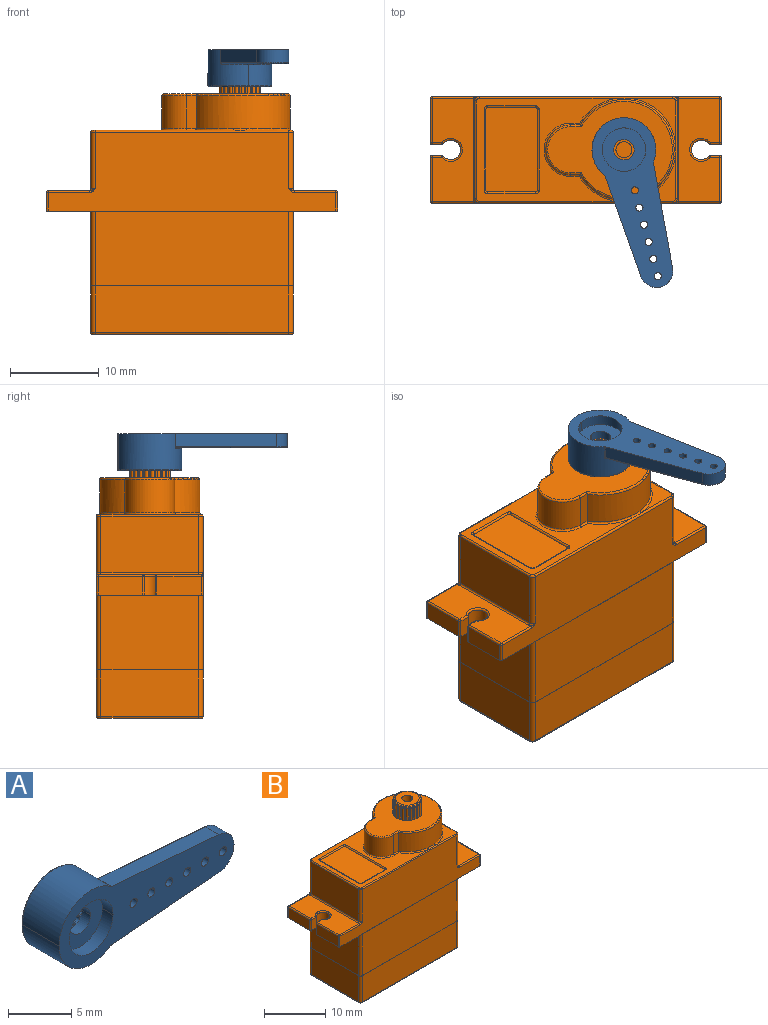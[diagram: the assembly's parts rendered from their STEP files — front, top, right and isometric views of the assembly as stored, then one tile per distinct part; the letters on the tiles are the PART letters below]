
ASSEMBLY  parts=2 mates=1
PART A: 128 faces, bbox 20x4.2x7.5 mm
  f0: plane 13.4x5.41mm, normal (0,1,0), area 47.5mm2, adj f1,f2,f3,f4,f5,f6,f7,f8
  f1: cylinder r=0.1mm len=12.05mm, axis (1,0,0.08), area 1.9mm2, adj f0,f2,f18,f20
  f2: torus R=1.75mm, axis (0,-1,0), area 0.8mm2, adj f0,f1,f3,f21
  f3: cylinder r=0.1mm len=12.05mm, axis (1,0,-0.08), area 1.9mm2, adj f0,f2,f16,f22
  f4: torus R=0.5mm, axis (0,-1,0), area 0.2mm2, adj f0,f5,f24
  f5: torus R=0.5mm, axis (0,-1,0), area 0.2mm2, adj f0,f4,f25
  f6: torus R=0.5mm, axis (0,-1,0), area 0.2mm2, adj f0,f7,f26
  f7: torus R=0.5mm, axis (0,-1,0), area 0.2mm2, adj f0,f6,f27
  f8: torus R=0.5mm, axis (0,-1,0), area 0.2mm2, adj f0,f9,f28
  f9: torus R=0.5mm, axis (0,-1,0), area 0.2mm2, adj f0,f8,f29
  f10: torus R=0.5mm, axis (0,-1,0), area 0.2mm2, adj f0,f11,f30
  f11: torus R=0.5mm, axis (0,-1,0), area 0.2mm2, adj f0,f10,f31
  f12: torus R=0.5mm, axis (0,-1,0), area 0.2mm2, adj f0,f13,f32
  f13: torus R=0.5mm, axis (0,-1,0), area 0.2mm2, adj f0,f12,f33
  f14: torus R=0.5mm, axis (0,-1,0), area 0.2mm2, adj f0,f15,f34
  f15: torus R=0.5mm, axis (0,-1,0), area 0.2mm2, adj f0,f14,f35
  f16: bspline ~0.32x0.22mm, area 0mm2, adj f3,f17,f23,f36
  f17: torus R=3.7mm, axis (0,-1,0), area 0.9mm2, adj f0,f16,f18,f36,f37
  f18: bspline ~0.32x0.22mm, area 0mm2, adj f1,f17,f19,f37
  f19: cylinder r=0.1mm len=1.5mm, axis (0,-1,0), area 0.1mm2, adj f18,f20,f37,f38
  f20: plane 12.04x1.5mm, normal (0.08,0,-1), area 18.1mm2, adj f1,f19,f21,f38
  f21: cylinder r=1.85mm len=3.69mm, axis (0,-1,0), area 8.3mm2, adj f2,f20,f22,f38
  f22: plane 12.04x1.5mm, normal (0.08,0,1), area 18.1mm2, adj f3,f21,f23,f38
  f23: cylinder r=0.1mm len=1.5mm, axis (0,1,0), area 0.1mm2, adj f16,f22,f36,f38
  f24: cylinder r=0.4mm len=1.5mm, axis (0,-1,0), area 1.9mm2, adj f4,f25,f38
  f25: cylinder r=0.4mm len=1.5mm, axis (0,-1,0), area 1.9mm2, adj f5,f24,f38
  f26: cylinder r=0.4mm len=1.5mm, axis (0,-1,0), area 1.9mm2, adj f6,f27,f38
  f27: cylinder r=0.4mm len=1.5mm, axis (0,-1,0), area 1.9mm2, adj f7,f26,f38
  f28: cylinder r=0.4mm len=1.5mm, axis (0,-1,0), area 1.9mm2, adj f8,f29,f38
  f29: cylinder r=0.4mm len=1.5mm, axis (0,-1,0), area 1.9mm2, adj f9,f28,f38
  f30: cylinder r=0.4mm len=1.5mm, axis (0,-1,0), area 1.9mm2, adj f10,f31,f38
  f31: cylinder r=0.4mm len=1.5mm, axis (0,-1,0), area 1.9mm2, adj f11,f30,f38
  f32: cylinder r=0.4mm len=1.5mm, axis (0,-1,0), area 1.9mm2, adj f12,f33,f38
  f33: cylinder r=0.4mm len=1.5mm, axis (0,-1,0), area 1.9mm2, adj f13,f32,f38
  f34: cylinder r=0.4mm len=1.5mm, axis (0,-1,0), area 1.9mm2, adj f14,f35,f38
  f35: cylinder r=0.4mm len=1.5mm, axis (0,-1,0), area 1.9mm2, adj f15,f34,f38
  f36: cylinder r=3.6mm len=7.2mm, axis (0,-1,0), area 40.8mm2, adj f16,f17,f23,f37,f38,f39
  f37: cylinder r=3.6mm len=7.2mm, axis (0,-1,0), area 40.8mm2, adj f17,f18,f19,f36,f38,f40
  f38: plane 19.63x7.27mm, normal (0,-1,0), area 74.7mm2, adj f19,f20,f21,f22,f23,f24,f25,f26
  f39: torus R=3.5mm, axis (0,-1,0), area 1.8mm2, adj f36,f40,f61
  f40: torus R=3.5mm, axis (0,-1,0), area 1.8mm2, adj f37,f39,f61
  f41: cylinder r=2.45mm len=4.9mm, axis (0,-1,0), area 9.2mm2, adj f38,f42,f64
  f42: cylinder r=2.45mm len=4.9mm, axis (0,-1,0), area 9.2mm2, adj f38,f41,f64
  f43: cone r=1.23mm half-angle=45deg, axis (0,1,0), area 0.1mm2, adj f61,f67,f68,f69,f70
  f44: cone r=1.23mm half-angle=45deg, axis (0,1,0), area 0.1mm2, adj f61,f70,f71,f72,f73
  f45: cone r=1.23mm half-angle=45deg, axis (0,1,0), area 0.1mm2, adj f61,f73,f74,f75,f76
  f46: cone r=1.23mm half-angle=45deg, axis (0,1,0), area 0.1mm2, adj f61,f76,f77,f78,f79
  f47: cone r=1.23mm half-angle=45deg, axis (0,1,0), area 0.1mm2, adj f61,f79,f80,f81,f82
  f48: cone r=1.23mm half-angle=45deg, axis (0,1,0), area 0.1mm2, adj f61,f82,f83,f84,f85
  f49: cone r=1.23mm half-angle=45deg, axis (0,1,0), area 0.1mm2, adj f61,f85,f86,f87,f88
  f50: cone r=1.23mm half-angle=45deg, axis (0,1,0), area 0.1mm2, adj f61,f88,f89,f90,f91
  f51: cone r=1.23mm half-angle=45deg, axis (0,1,0), area 0.1mm2, adj f61,f91,f92,f93,f94
  f52: cone r=1.23mm half-angle=45deg, axis (0,1,0), area 0.1mm2, adj f61,f94,f95,f96,f97
  f53: cone r=1.23mm half-angle=45deg, axis (0,1,0), area 0.1mm2, adj f61,f97,f98,f99,f100
  f54: cone r=1.23mm half-angle=45deg, axis (0,1,0), area 0.1mm2, adj f61,f100,f101,f102,f103
  f55: cone r=1.23mm half-angle=45deg, axis (0,1,0), area 0.1mm2, adj f61,f103,f104,f105,f106
  f56: cone r=1.23mm half-angle=45deg, axis (0,1,0), area 0.1mm2, adj f61,f106,f107,f108,f109
  f57: cone r=1.23mm half-angle=45deg, axis (0,1,0), area 0.1mm2, adj f61,f109,f110,f111,f112
  f58: cone r=1.23mm half-angle=45deg, axis (0,1,0), area 0.1mm2, adj f61,f112,f113,f114,f115
  f59: cone r=1.23mm half-angle=45deg, axis (0,1,0), area 0.1mm2, adj f61,f115,f116,f117,f118
  f60: cone r=1.23mm half-angle=45deg, axis (0,1,0), area 0.1mm2, adj f61,f118,f119,f120,f121
  f61: plane 7.13x7mm, normal (0,1,0), area 21.3mm2, adj f39,f40,f43,f44,f45,f46,f47,f48
  f62: cone r=1.23mm half-angle=45deg, axis (0,1,0), area 0.1mm2, adj f61,f65,f66,f67,f124
  f63: cone r=1.23mm half-angle=45deg, axis (0,1,0), area 0.1mm2, adj f61,f121,f122,f123,f124
  f64: plane 4.99x4.9mm, normal (0,-1,0), area 14.7mm2, adj f41,f42,f125,f126
  f65: cylinder r=0.17mm len=1.9mm, axis (0,-1,0), area 0.3mm2, adj f62,f66,f124,f127
  f66: cylinder r=0.17mm len=1.9mm, axis (0,-1,0), area 0.3mm2, adj f62,f65,f67,f127
  f67: cylinder r=0.24mm len=2mm, axis (0,-1,0), area 1mm2, adj f43,f61,f62,f66,f68,f127
  f68: cylinder r=0.17mm len=1.9mm, axis (0,-1,0), area 0.3mm2, adj f43,f67,f69,f127
  f69: cylinder r=0.17mm len=1.9mm, axis (0,-1,0), area 0.3mm2, adj f43,f68,f70,f127
  f70: cylinder r=0.24mm len=2mm, axis (0,-1,0), area 1mm2, adj f43,f44,f61,f69,f71,f127
  f71: cylinder r=0.17mm len=1.9mm, axis (0,-1,0), area 0.3mm2, adj f44,f70,f72,f127
  f72: cylinder r=0.17mm len=1.9mm, axis (0,-1,0), area 0.3mm2, adj f44,f71,f73,f127
  f73: cylinder r=0.24mm len=2mm, axis (0,-1,0), area 1mm2, adj f44,f45,f61,f72,f74,f127
  f74: cylinder r=0.17mm len=1.9mm, axis (0,-1,0), area 0.3mm2, adj f45,f73,f75,f127
  f75: cylinder r=0.17mm len=1.9mm, axis (0,-1,0), area 0.3mm2, adj f45,f74,f76,f127
  f76: cylinder r=0.24mm len=2mm, axis (0,-1,0), area 1mm2, adj f45,f46,f61,f75,f77,f127
  f77: cylinder r=0.17mm len=1.9mm, axis (0,-1,0), area 0.3mm2, adj f46,f76,f78,f127
  f78: cylinder r=0.17mm len=1.9mm, axis (0,-1,0), area 0.3mm2, adj f46,f77,f79,f127
  f79: cylinder r=0.24mm len=2mm, axis (0,-1,0), area 1mm2, adj f46,f47,f61,f78,f80,f127
  f80: cylinder r=0.17mm len=1.9mm, axis (0,-1,0), area 0.3mm2, adj f47,f79,f81,f127
  f81: cylinder r=0.17mm len=1.9mm, axis (0,-1,0), area 0.3mm2, adj f47,f80,f82,f127
  f82: cylinder r=0.24mm len=2mm, axis (0,-1,0), area 1mm2, adj f47,f48,f61,f81,f83,f127
  f83: cylinder r=0.17mm len=1.9mm, axis (0,-1,0), area 0.3mm2, adj f48,f82,f84,f127
  f84: cylinder r=0.17mm len=1.9mm, axis (0,-1,0), area 0.3mm2, adj f48,f83,f85,f127
  f85: cylinder r=0.24mm len=2mm, axis (0,-1,0), area 1mm2, adj f48,f49,f61,f84,f86,f127
  f86: cylinder r=0.17mm len=1.9mm, axis (0,-1,0), area 0.3mm2, adj f49,f85,f87,f127
  f87: cylinder r=0.17mm len=1.9mm, axis (0,-1,0), area 0.3mm2, adj f49,f86,f88,f127
  f88: cylinder r=0.24mm len=2mm, axis (0,-1,0), area 1mm2, adj f49,f50,f61,f87,f89,f127
  f89: cylinder r=0.17mm len=1.9mm, axis (0,-1,0), area 0.3mm2, adj f50,f88,f90,f127
  f90: cylinder r=0.17mm len=1.9mm, axis (0,-1,0), area 0.3mm2, adj f50,f89,f91,f127
  f91: cylinder r=0.24mm len=2mm, axis (0,-1,0), area 1mm2, adj f50,f51,f61,f90,f92,f127
  f92: cylinder r=0.17mm len=1.9mm, axis (0,-1,0), area 0.3mm2, adj f51,f91,f93,f127
  f93: cylinder r=0.17mm len=1.9mm, axis (0,-1,0), area 0.3mm2, adj f51,f92,f94,f127
  f94: cylinder r=0.24mm len=2mm, axis (0,-1,0), area 1mm2, adj f51,f52,f61,f93,f95,f127
  f95: cylinder r=0.17mm len=1.9mm, axis (0,-1,0), area 0.3mm2, adj f52,f94,f96,f127
  f96: cylinder r=0.17mm len=1.9mm, axis (0,-1,0), area 0.3mm2, adj f52,f95,f97,f127
  f97: cylinder r=0.24mm len=2mm, axis (0,-1,0), area 1mm2, adj f52,f53,f61,f96,f98,f127
  f98: cylinder r=0.17mm len=1.9mm, axis (0,-1,0), area 0.3mm2, adj f53,f97,f99,f127
  f99: cylinder r=0.17mm len=1.9mm, axis (0,-1,0), area 0.3mm2, adj f53,f98,f100,f127
  f100: cylinder r=0.24mm len=2mm, axis (0,-1,0), area 1mm2, adj f53,f54,f61,f99,f101,f127
  f101: cylinder r=0.17mm len=1.9mm, axis (0,-1,0), area 0.3mm2, adj f54,f100,f102,f127
  f102: cylinder r=0.17mm len=1.9mm, axis (0,-1,0), area 0.3mm2, adj f54,f101,f103,f127
  f103: cylinder r=0.24mm len=2mm, axis (0,-1,0), area 1mm2, adj f54,f55,f61,f102,f104,f127
  f104: cylinder r=0.17mm len=1.9mm, axis (0,-1,0), area 0.3mm2, adj f55,f103,f105,f127
  f105: cylinder r=0.17mm len=1.9mm, axis (0,-1,0), area 0.3mm2, adj f55,f104,f106,f127
  f106: cylinder r=0.24mm len=2mm, axis (0,-1,0), area 1mm2, adj f55,f56,f61,f105,f107,f127
  f107: cylinder r=0.17mm len=1.9mm, axis (0,-1,0), area 0.3mm2, adj f56,f106,f108,f127
  f108: cylinder r=0.17mm len=1.9mm, axis (0,-1,0), area 0.3mm2, adj f56,f107,f109,f127
  f109: cylinder r=0.24mm len=2mm, axis (0,-1,0), area 1mm2, adj f56,f57,f61,f108,f110,f127
  f110: cylinder r=0.17mm len=1.9mm, axis (0,-1,0), area 0.3mm2, adj f57,f109,f111,f127
  f111: cylinder r=0.17mm len=1.9mm, axis (0,-1,0), area 0.3mm2, adj f57,f110,f112,f127
  f112: cylinder r=0.24mm len=2mm, axis (0,-1,0), area 1mm2, adj f57,f58,f61,f111,f113,f127
  f113: cylinder r=0.17mm len=1.9mm, axis (0,-1,0), area 0.3mm2, adj f58,f112,f114,f127
  f114: cylinder r=0.17mm len=1.9mm, axis (0,-1,0), area 0.3mm2, adj f58,f113,f115,f127
  f115: cylinder r=0.24mm len=2mm, axis (0,-1,0), area 1mm2, adj f58,f59,f61,f114,f116,f127
  f116: cylinder r=0.17mm len=1.9mm, axis (0,-1,0), area 0.3mm2, adj f59,f115,f117,f127
  f117: cylinder r=0.17mm len=1.9mm, axis (0,-1,0), area 0.3mm2, adj f59,f116,f118,f127
  f118: cylinder r=0.24mm len=2mm, axis (0,-1,0), area 1mm2, adj f59,f60,f61,f117,f119,f127
  f119: cylinder r=0.17mm len=1.9mm, axis (0,-1,0), area 0.3mm2, adj f60,f118,f120,f127
  f120: cylinder r=0.17mm len=1.9mm, axis (0,-1,0), area 0.3mm2, adj f60,f119,f121,f127
  f121: cylinder r=0.24mm len=2mm, axis (0,-1,0), area 1mm2, adj f60,f61,f63,f120,f122,f127
  f122: cylinder r=0.17mm len=1.9mm, axis (0,-1,0), area 0.3mm2, adj f63,f121,f123,f127
  f123: cylinder r=0.17mm len=1.9mm, axis (0,-1,0), area 0.3mm2, adj f63,f122,f124,f127
  f124: cylinder r=0.24mm len=2mm, axis (0,-1,0), area 1mm2, adj f61,f62,f63,f65,f123,f127
  f125: cylinder r=1.15mm len=2.3mm, axis (0,-1,0), area 3.6mm2, adj f64,f126,f127
  f126: cylinder r=1.15mm len=2.3mm, axis (0,-1,0), area 3.6mm2, adj f64,f125,f127
  f127: plane 4.65x4.65mm, normal (0,1,0), area 11.9mm2, adj f65,f66,f67,f68,f69,f70,f71,f72
PART B: 213 faces, bbox 32.8x12.9x29.9 mm
  f0: plane 22.4x11.6mm, normal (0,0,-1), area 259.8mm2, adj f1,f2,f3,f4,f5,f6,f7,f8
  f1: torus R=0.3mm, axis (0,0,1), area 0.2mm2, adj f0,f2,f8,f9
  f2: cylinder r=0.2mm len=11mm, axis (0,1,0), area 3.5mm2, adj f0,f1,f3,f10
  f3: torus R=0.3mm, axis (0,0,1), area 0.2mm2, adj f0,f2,f4,f11
  f4: cylinder r=0.2mm len=21.8mm, axis (1,0,0), area 6.8mm2, adj f0,f3,f5,f12
  f5: torus R=0.3mm, axis (0,0,1), area 0.2mm2, adj f0,f4,f6,f13
  f6: cylinder r=0.2mm len=11mm, axis (0,-1,0), area 3.5mm2, adj f0,f5,f7,f14
  f7: torus R=0.3mm, axis (0,0,1), area 0.2mm2, adj f0,f6,f8,f15
  f8: cylinder r=0.2mm len=21.8mm, axis (1,0,0), area 6.8mm2, adj f0,f1,f7,f16
  f9: cylinder r=0.5mm len=5.28mm, axis (0,0,1), area 4.1mm2, adj f1,f10,f16,f17
  f10: plane 11x5.28mm, normal (1,0,0), area 58.1mm2, adj f2,f9,f11,f17
  f11: cylinder r=0.5mm len=5.28mm, axis (0,0,1), area 4.1mm2, adj f3,f10,f12,f17
  f12: plane 21.8x5.28mm, normal (0,1,0), area 115.1mm2, adj f4,f11,f13,f17
  f13: cylinder r=0.5mm len=5.28mm, axis (0,0,1), area 4.1mm2, adj f5,f12,f14,f17
  f14: plane 11x5.28mm, normal (-1,0,0), area 58.1mm2, adj f6,f13,f15,f17
  f15: cylinder r=0.5mm len=5.28mm, axis (0,0,1), area 4.1mm2, adj f7,f14,f16,f17
  f16: plane 21.8x5.28mm, normal (0,-1,0), area 115.1mm2, adj f8,f9,f15,f17
  f17: plane 22.8x12mm, normal (0,0,1), area 13.6mm2, adj f9,f10,f11,f12,f13,f14,f15,f16
  f18: cylinder r=0.3mm len=0.3mm, axis (0,0,1), area 0mm2, adj f17,f19,f25,f26
  f19: plane 11x0.02mm, normal (1,0,0), area 0.2mm2, adj f17,f18,f20,f26
  f20: cylinder r=0.3mm len=0.3mm, axis (0,0,1), area 0mm2, adj f17,f19,f21,f26
  f21: plane 21.8x0.02mm, normal (0,-1,0), area 0.4mm2, adj f17,f20,f22,f26
  f22: cylinder r=0.3mm len=0.3mm, axis (0,0,1), area 0mm2, adj f17,f21,f23,f26
  f23: plane 11x0.02mm, normal (-1,0,0), area 0.2mm2, adj f17,f22,f24,f26
  f24: cylinder r=0.3mm len=0.3mm, axis (0,0,1), area 0mm2, adj f17,f23,f25,f26
  f25: plane 21.8x0.02mm, normal (0,1,0), area 0.4mm2, adj f17,f18,f24,f26
  f26: plane 22.8x12mm, normal (0,0,-1), area 13.6mm2, adj f18,f19,f20,f21,f22,f23,f24,f25
  f27: cylinder r=0.5mm len=8.38mm, axis (0,0,1), area 6.6mm2, adj f26,f28,f34,f39
  f28: plane 11x8.38mm, normal (1,0,0), area 92.2mm2, adj f26,f27,f29,f39
  f29: cylinder r=0.5mm len=8.38mm, axis (0,0,1), area 6.6mm2, adj f26,f28,f30,f39
  f30: plane 21.8x8.38mm, normal (0,1,0), area 182.7mm2, adj f26,f29,f31,f39
  f31: cylinder r=0.5mm len=8.38mm, axis (0,0,1), area 6.6mm2, adj f26,f30,f32,f39
  f32: plane 11x8.38mm, normal (-1,0,0), area 92.2mm2, adj f26,f31,f33,f39
  f33: cylinder r=0.5mm len=8.38mm, axis (0,0,1), area 6.6mm2, adj f26,f32,f34,f39
  f34: plane 21.8x8.38mm, normal (0,-1,0), area 182.7mm2, adj f26,f27,f33,f39
  f35: sphere r=0.2mm, area 0.1mm2, adj f45,f49,f53
  f36: sphere r=0.2mm, area 0.1mm2, adj f47,f48,f57
  f37: sphere r=0.2mm, area 0mm2, adj f41,f42,f60
  f38: sphere r=0.2mm, area 0.1mm2, adj f40,f44,f64
  f39: plane 22.8x12mm, normal (0,0,1), area 13.6mm2, adj f27,f28,f29,f30,f31,f32,f33,f34
  f40: cylinder r=0.2mm len=5mm, axis (0,-1,0), area 1.6mm2, adj f38,f73,f74,f75
  f41: cylinder r=0.2mm len=5mm, axis (0,-1,0), area 1.6mm2, adj f37,f51,f59,f75
  f42: cylinder r=0.2mm len=1.18mm, axis (-1,0,0), area 0.4mm2, adj f37,f43,f61,f75
  f43: torus R=1.3mm, axis (0,0,-1), area 1.9mm2, adj f42,f44,f62,f75
  f44: cylinder r=0.2mm len=1.18mm, axis (-1,0,0), area 0.4mm2, adj f38,f43,f63,f75
  f45: cylinder r=0.2mm len=1.18mm, axis (-1,0,0), area 0.4mm2, adj f35,f46,f54,f77
  f46: torus R=1.3mm, axis (0,0,-1), area 1.9mm2, adj f45,f47,f55,f77
  f47: cylinder r=0.2mm len=1.18mm, axis (-1,0,0), area 0.4mm2, adj f36,f46,f56,f77
  f48: cylinder r=0.2mm len=5mm, axis (0,-1,0), area 1.6mm2, adj f36,f50,f58,f77
  f49: cylinder r=0.2mm len=5mm, axis (0,-1,0), area 1.6mm2, adj f35,f77,f78,f79
  f50: sphere r=0.2mm, area 0mm2, adj f48,f83,f84
  f51: sphere r=0.2mm, area 0.1mm2, adj f41,f87,f88
  f52: torus R=0.7mm, axis (0,0,-1), area 0.2mm2, adj f77,f85,f89,f90
  f53: cylinder r=0.2mm len=2.1mm, axis (0,0,1), area 0.7mm2, adj f35,f54,f79,f91
  f54: plane 2.1x1.18mm, normal (0,-1,0), area 2.5mm2, adj f45,f53,f55,f91
  f55: cylinder r=1.1mm len=2.2mm, axis (0,0,1), area 11.8mm2, adj f46,f54,f56,f91
  f56: plane 2.1x1.18mm, normal (0,1,0), area 2.5mm2, adj f47,f55,f57,f91
  f57: cylinder r=0.2mm len=2.1mm, axis (0,0,-1), area 0.7mm2, adj f36,f56,f58,f91
  f58: plane 5x2.1mm, normal (1,0,0), area 10.5mm2, adj f48,f57,f83,f91
  f59: plane 5x2.1mm, normal (-1,0,0), area 10.5mm2, adj f41,f60,f88,f91
  f60: cylinder r=0.2mm len=2.1mm, axis (0,0,1), area 0.7mm2, adj f37,f59,f61,f91
  f61: plane 2.1x1.18mm, normal (0,1,0), area 2.5mm2, adj f42,f60,f62,f91
  f62: cylinder r=1.1mm len=2.2mm, axis (0,0,1), area 11.8mm2, adj f43,f61,f63,f91
  f63: plane 2.1x1.18mm, normal (0,-1,0), area 2.5mm2, adj f44,f62,f64,f91
  f64: cylinder r=0.2mm len=2.1mm, axis (0,0,1), area 0.7mm2, adj f38,f63,f73,f91
  f65: cylinder r=0.3mm len=0.3mm, axis (0,0,1), area 0mm2, adj f39,f66,f72,f91
  f66: plane 21.8x0.02mm, normal (0,1,0), area 0.4mm2, adj f39,f65,f67,f91
  f67: cylinder r=0.3mm len=0.3mm, axis (0,0,1), area 0mm2, adj f39,f66,f68,f91
  f68: plane 11x0.02mm, normal (-1,0,0), area 0.2mm2, adj f39,f67,f69,f91
  f69: cylinder r=0.3mm len=0.3mm, axis (0,0,1), area 0mm2, adj f39,f68,f70,f91
  f70: plane 21.8x0.02mm, normal (0,-1,0), area 0.4mm2, adj f39,f69,f71,f91
  f71: cylinder r=0.3mm len=0.3mm, axis (0,0,1), area 0mm2, adj f39,f70,f72,f91
  f72: plane 11x0.02mm, normal (1,0,0), area 0.2mm2, adj f39,f65,f71,f91
  f73: plane 5x2.1mm, normal (-1,0,0), area 10.5mm2, adj f40,f64,f91,f92
  f74: sphere r=0.2mm, area 0.1mm2, adj f40,f92,f93
  f75: plane 11.6x4.67mm, normal (0,0,1), area 46.6mm2, adj f40,f41,f42,f43,f44,f80,f81,f82
  f76: torus R=0.7mm, axis (0,0,-1), area 0.2mm2, adj f77,f90,f95,f96
  f77: plane 11.6x4.67mm, normal (0,0,1), area 46.6mm2, adj f45,f46,f47,f48,f49,f52,f76,f84
  f78: sphere r=0.2mm, area 0.1mm2, adj f49,f97,f98
  f79: plane 5x2.1mm, normal (1,0,0), area 10.5mm2, adj f49,f53,f91,f98
  f80: torus R=0.7mm, axis (0,0,-1), area 0.2mm2, adj f75,f81,f94,f99
  f81: cylinder r=0.2mm len=11mm, axis (0,1,0), area 3.5mm2, adj f75,f80,f82,f100
  f82: torus R=0.7mm, axis (0,0,-1), area 0.2mm2, adj f75,f81,f86,f101
  f83: cylinder r=0.2mm len=2.1mm, axis (0,0,1), area 0.7mm2, adj f50,f58,f91,f103
  f84: cylinder r=0.2mm len=4.67mm, axis (1,0,0), area 1.5mm2, adj f50,f77,f85,f103
  f85: bspline ~0.63x0.4mm, area 0.1mm2, adj f52,f84,f103
  f86: bspline ~0.63x0.4mm, area 0.1mm2, adj f82,f87,f103
  f87: cylinder r=0.2mm len=4.67mm, axis (1,0,0), area 1.5mm2, adj f51,f75,f86,f103
  f88: cylinder r=0.2mm len=2.1mm, axis (0,0,-1), area 0.7mm2, adj f51,f59,f91,f103
  f89: cylinder r=0.5mm len=6.4mm, axis (0,0,1), area 5mm2, adj f52,f103,f104,f105
  f90: cylinder r=0.2mm len=11mm, axis (0,-1,0), area 3.5mm2, adj f52,f76,f77,f105
  f91: plane 32.8x12mm, normal (0,0,-1), area 123.1mm2, adj f53,f54,f55,f56,f57,f58,f59,f60
  f92: cylinder r=0.2mm len=2.1mm, axis (0,0,1), area 0.7mm2, adj f73,f74,f91,f107
  f93: cylinder r=0.2mm len=4.67mm, axis (1,0,0), area 1.5mm2, adj f74,f75,f94,f107
  f94: bspline ~0.63x0.4mm, area 0.1mm2, adj f80,f93,f107
  f95: cylinder r=0.5mm len=6.4mm, axis (0,0,1), area 5mm2, adj f76,f105,f106,f107
  f96: bspline ~0.63x0.4mm, area 0.1mm2, adj f76,f97,f107
  f97: cylinder r=0.2mm len=4.67mm, axis (1,0,0), area 1.5mm2, adj f77,f78,f96,f107
  f98: cylinder r=0.2mm len=2.1mm, axis (0,0,-1), area 0.7mm2, adj f78,f79,f91,f107
  f99: cylinder r=0.5mm len=6.4mm, axis (0,0,1), area 5mm2, adj f80,f100,f107,f108
  f100: plane 11x6.4mm, normal (-1,0,0), area 70.4mm2, adj f81,f99,f101,f109
  f101: cylinder r=0.5mm len=6.4mm, axis (0,0,1), area 5mm2, adj f82,f100,f103,f110
  f102: plane 9.5x5.8mm, normal (0,0,1), area 55.1mm2, adj f111,f112,f113,f114,f115,f116,f117,f118
  f103: plane 32.4x8.9mm, normal (0,-1,0), area 216.4mm2, adj f83,f84,f85,f86,f87,f88,f89,f91
  f104: torus R=0.3mm, axis (0,0,1), area 0.2mm2, adj f89,f119,f120,f121
  f105: plane 11x6.4mm, normal (1,0,0), area 70.4mm2, adj f89,f90,f95,f121
  f106: torus R=0.3mm, axis (0,0,1), area 0.2mm2, adj f95,f121,f122,f123
  f107: plane 32.4x8.9mm, normal (0,1,0), area 216.4mm2, adj f91,f92,f93,f94,f95,f96,f97,f98
  f108: torus R=0.3mm, axis (0,0,1), area 0.2mm2, adj f99,f109,f123,f124
  f109: cylinder r=0.2mm len=11mm, axis (0,1,0), area 3.5mm2, adj f100,f108,f110,f124
  f110: torus R=0.3mm, axis (0,0,1), area 0.2mm2, adj f101,f109,f119,f124
  f111: torus R=0.4mm, axis (0,0,1), area 0.1mm2, adj f102,f112,f118,f124
  f112: cylinder r=0.2mm len=5.4mm, axis (-1,0,0), area 1.7mm2, adj f102,f111,f113,f124
  f113: torus R=0.4mm, axis (0,0,1), area 0.1mm2, adj f102,f112,f114,f124
  f114: cylinder r=0.2mm len=9.1mm, axis (0,1,0), area 2.9mm2, adj f102,f113,f115,f124
  f115: torus R=0.4mm, axis (0,0,1), area 0.1mm2, adj f102,f114,f116,f124
  f116: cylinder r=0.2mm len=5.4mm, axis (1,0,0), area 1.7mm2, adj f102,f115,f117,f124
  f117: torus R=0.4mm, axis (0,0,1), area 0.1mm2, adj f102,f116,f118,f124
  f118: cylinder r=0.2mm len=9.1mm, axis (0,-1,0), area 2.9mm2, adj f102,f111,f117,f124
  f119: cylinder r=0.2mm len=21.8mm, axis (-1,0,0), area 6.8mm2, adj f103,f104,f110,f120,f124,f129
  f120: plane 5.04x5.04mm, normal (0,0,1), area 6.8mm2, adj f104,f119,f121,f130
  f121: cylinder r=0.2mm len=11mm, axis (0,-1,0), area 3.4mm2, adj f104,f105,f106,f120,f122,f131
  f122: plane 5.04x5.04mm, normal (0,0,1), area 6.8mm2, adj f106,f121,f123,f132
  f123: cylinder r=0.2mm len=21.8mm, axis (1,0,0), area 6.8mm2, adj f106,f107,f108,f122,f124,f133
  f124: plane 15.84x11.6mm, normal (0,0,1), area 60.9mm2, adj f108,f109,f110,f111,f112,f113,f114,f115
  f125: cylinder r=0.2mm len=1.09mm, axis (1,0,0), area 0.3mm2, adj f124,f126,f134,f135
  f126: torus R=3mm, axis (0,0,1), area 2.8mm2, adj f124,f125,f127,f136
  f127: cylinder r=0.2mm len=1.09mm, axis (1,0,0), area 0.3mm2, adj f124,f126,f128,f137
  f128: torus R=5.85mm, axis (0,0,1), area 1.6mm2, adj f124,f127,f129,f138
  f129: bspline ~1.53x0.22mm, area 0.4mm2, adj f119,f128,f130,f138
  f130: torus R=5.85mm, axis (0,0,1), area 2.4mm2, adj f120,f129,f131,f138
  f131: bspline ~1.53x0.22mm, area 0.4mm2, adj f121,f130,f132,f138
  f132: torus R=5.85mm, axis (0,0,1), area 2.4mm2, adj f122,f131,f133,f138
  f133: bspline ~1.53x0.22mm, area 0.4mm2, adj f123,f132,f134,f138
  f134: torus R=5.85mm, axis (0,0,1), area 1.6mm2, adj f124,f125,f133,f138
  f135: plane 3.7x1.09mm, normal (0,1,0), area 4mm2, adj f125,f136,f138,f139
  f136: cylinder r=2.8mm len=5.6mm, axis (0,0,1), area 32.5mm2, adj f126,f135,f137,f140
  f137: plane 3.7x1.09mm, normal (0,-1,0), area 4mm2, adj f127,f136,f138,f141
  f138: cylinder r=5.65mm len=11.3mm, axis (0,0,1), area 109.7mm2, adj f128,f129,f130,f131,f132,f133,f134,f135
  f139: cylinder r=0.2mm len=1.21mm, axis (-1,0,0), area 0.4mm2, adj f135,f140,f142,f143
  f140: torus R=2.6mm, axis (0,0,1), area 2.7mm2, adj f136,f139,f141,f143
  f141: cylinder r=0.2mm len=1.21mm, axis (1,0,0), area 0.4mm2, adj f137,f140,f142,f143
  f142: torus R=5.45mm, axis (0,0,1), area 9.2mm2, adj f138,f139,f141,f143
  f143: plane 14.17x11.04mm, normal (0,0,1), area 89.8mm2, adj f139,f140,f141,f142,f144,f145
  f144: cylinder r=2.4mm len=4.8mm, axis (0,0,1), area 1.5mm2, adj f143,f145,f146
  f145: cylinder r=2.4mm len=4.8mm, axis (0,0,1), area 1.5mm2, adj f143,f144,f146
  f146: plane 4.89x4.8mm, normal (0,0,1), area 2mm2, adj f144,f145,f147,f148,f149,f150,f151,f152
  f147: cylinder r=0.17mm len=2.94mm, axis (0,0,1), area 0.5mm2, adj f146,f148,f175,f207
  f148: cylinder r=0.17mm len=2.94mm, axis (0,0,1), area 0.5mm2, adj f146,f147,f149,f207
  f149: cylinder r=0.24mm len=2.88mm, axis (0,0,1), area 1.4mm2, adj f146,f148,f150,f207
  f150: cylinder r=0.17mm len=2.94mm, axis (0,0,1), area 0.5mm2, adj f146,f149,f151,f207
  f151: cylinder r=0.17mm len=2.94mm, axis (0,0,1), area 0.5mm2, adj f146,f150,f152,f207
  f152: cylinder r=0.24mm len=2.88mm, axis (0,0,1), area 1.4mm2, adj f146,f151,f153,f207
  f153: cylinder r=0.17mm len=2.94mm, axis (0,0,1), area 0.5mm2, adj f146,f152,f154,f207
  f154: cylinder r=0.17mm len=2.94mm, axis (0,0,1), area 0.5mm2, adj f146,f153,f155,f207
  f155: cylinder r=0.24mm len=2.88mm, axis (0,0,1), area 1.4mm2, adj f146,f154,f156,f207
  f156: cylinder r=0.17mm len=2.94mm, axis (0,0,1), area 0.5mm2, adj f146,f155,f157,f207
  f157: cylinder r=0.17mm len=2.94mm, axis (0,0,1), area 0.5mm2, adj f146,f156,f158,f207
  f158: cylinder r=0.24mm len=2.88mm, axis (0,0,1), area 1.4mm2, adj f146,f157,f159,f207
  f159: cylinder r=0.17mm len=2.94mm, axis (0,0,1), area 0.5mm2, adj f146,f158,f160,f207
  f160: cylinder r=0.17mm len=2.94mm, axis (0,0,1), area 0.5mm2, adj f146,f159,f161,f207
  f161: cylinder r=0.24mm len=2.88mm, axis (0,0,1), area 1.4mm2, adj f146,f160,f162,f207
  f162: cylinder r=0.17mm len=2.94mm, axis (0,0,1), area 0.5mm2, adj f146,f161,f163,f207
  f163: cylinder r=0.17mm len=2.94mm, axis (0,0,1), area 0.5mm2, adj f146,f162,f164,f207
  f164: cylinder r=0.24mm len=2.88mm, axis (0,0,1), area 1.4mm2, adj f146,f163,f165,f207
  f165: cylinder r=0.17mm len=2.94mm, axis (0,0,1), area 0.5mm2, adj f146,f164,f166,f207
  f166: cylinder r=0.17mm len=2.94mm, axis (0,0,1), area 0.5mm2, adj f146,f165,f167,f207
  f167: cylinder r=0.24mm len=2.88mm, axis (0,0,1), area 1.4mm2, adj f146,f166,f168,f207
  f168: cylinder r=0.17mm len=2.94mm, axis (0,0,1), area 0.5mm2, adj f146,f167,f169,f207
  f169: cylinder r=0.17mm len=2.94mm, axis (0,0,1), area 0.5mm2, adj f146,f168,f170,f207
  f170: cylinder r=0.24mm len=2.88mm, axis (0,0,1), area 1.4mm2, adj f146,f169,f171,f207
  f171: cylinder r=0.17mm len=2.94mm, axis (0,0,1), area 0.5mm2, adj f146,f170,f172,f207
  f172: cylinder r=0.17mm len=2.94mm, axis (0,0,1), area 0.5mm2, adj f146,f171,f203,f207
  f173: cylinder r=0.17mm len=2.94mm, axis (0,0,1), area 0.5mm2, adj f146,f174,f202,f207
  f174: cylinder r=0.17mm len=2.94mm, axis (0,0,1), area 0.5mm2, adj f146,f173,f175,f207
  f175: cylinder r=0.24mm len=2.88mm, axis (0,0,1), area 1.4mm2, adj f146,f147,f174,f207
  f176: cylinder r=0.17mm len=2.94mm, axis (0,0,1), area 0.5mm2, adj f146,f177,f206,f208
  f177: cylinder r=0.17mm len=2.94mm, axis (0,0,1), area 0.5mm2, adj f146,f176,f178,f208
  f178: cylinder r=0.24mm len=2.88mm, axis (0,0,1), area 1.4mm2, adj f146,f177,f179,f208
  f179: cylinder r=0.17mm len=2.94mm, axis (0,0,1), area 0.5mm2, adj f146,f178,f180,f208
  f180: cylinder r=0.17mm len=2.94mm, axis (0,0,1), area 0.5mm2, adj f146,f179,f181,f208
  f181: cylinder r=0.24mm len=2.88mm, axis (0,0,1), area 1.4mm2, adj f146,f180,f182,f208
  f182: cylinder r=0.17mm len=2.94mm, axis (0,0,1), area 0.5mm2, adj f146,f181,f183,f208
  f183: cylinder r=0.17mm len=2.94mm, axis (0,0,1), area 0.5mm2, adj f146,f182,f184,f208
  f184: cylinder r=0.24mm len=2.88mm, axis (0,0,1), area 1.4mm2, adj f146,f183,f185,f208
  f185: cylinder r=0.17mm len=2.94mm, axis (0,0,1), area 0.5mm2, adj f146,f184,f186,f208
  f186: cylinder r=0.17mm len=2.94mm, axis (0,0,1), area 0.5mm2, adj f146,f185,f187,f208
  f187: cylinder r=0.24mm len=2.88mm, axis (0,0,1), area 1.4mm2, adj f146,f186,f188,f208
  f188: cylinder r=0.17mm len=2.94mm, axis (0,0,1), area 0.5mm2, adj f146,f187,f189,f208
  f189: cylinder r=0.17mm len=2.94mm, axis (0,0,1), area 0.5mm2, adj f146,f188,f190,f208
  f190: cylinder r=0.24mm len=2.88mm, axis (0,0,1), area 1.4mm2, adj f146,f189,f191,f208
  f191: cylinder r=0.17mm len=2.94mm, axis (0,0,1), area 0.5mm2, adj f146,f190,f192,f208
  f192: cylinder r=0.17mm len=2.94mm, axis (0,0,1), area 0.5mm2, adj f146,f191,f193,f208
  f193: cylinder r=0.24mm len=2.88mm, axis (0,0,1), area 1.4mm2, adj f146,f192,f194,f208
  f194: cylinder r=0.17mm len=2.94mm, axis (0,0,1), area 0.5mm2, adj f146,f193,f195,f208
  f195: cylinder r=0.17mm len=2.94mm, axis (0,0,1), area 0.5mm2, adj f146,f194,f196,f208
  f196: cylinder r=0.24mm len=2.88mm, axis (0,0,1), area 1.4mm2, adj f146,f195,f197,f208
  f197: cylinder r=0.17mm len=2.94mm, axis (0,0,1), area 0.5mm2, adj f146,f196,f198,f208
  f198: cylinder r=0.17mm len=2.94mm, axis (0,0,1), area 0.5mm2, adj f146,f197,f199,f208
  f199: cylinder r=0.24mm len=2.88mm, axis (0,0,1), area 1.4mm2, adj f146,f198,f200,f208
  f200: cylinder r=0.17mm len=2.94mm, axis (0,0,1), area 0.5mm2, adj f146,f199,f201,f208
  f201: cylinder r=0.17mm len=2.94mm, axis (0,0,1), area 0.5mm2, adj f146,f200,f202,f208
  f202: cylinder r=0.24mm len=2.88mm, axis (0,0,1), area 1.4mm2, adj f146,f173,f201,f207,f208
  f203: cylinder r=0.24mm len=2.88mm, axis (0,0,1), area 1.4mm2, adj f146,f172,f204,f207,f208
  f204: cylinder r=0.17mm len=2.94mm, axis (0,0,1), area 0.5mm2, adj f146,f203,f205,f208
  f205: cylinder r=0.17mm len=2.94mm, axis (0,0,1), area 0.5mm2, adj f146,f204,f206,f208
  f206: cylinder r=0.24mm len=2.88mm, axis (0,0,1), area 1.4mm2, adj f146,f176,f205,f208
  f207: torus R=1.95mm, axis (0,0,1), area 2.6mm2, adj f147,f148,f149,f150,f151,f152,f153,f154
  f208: torus R=1.95mm, axis (0,0,1), area 2.6mm2, adj f176,f177,f178,f179,f180,f181,f182,f183
  f209: plane 1.83x1.8mm, normal (0,0,1), area 2.5mm2, adj f210,f212
  f210: cylinder r=0.9mm len=3mm, axis (0,0,1), area 8.5mm2, adj f209,f211,f212
  f211: plane 3.95x3.95mm, normal (0,0,1), area 9.4mm2, adj f207,f208,f210,f212
  f212: cylinder r=0.9mm len=3mm, axis (0,0,1), area 8.5mm2, adj f209,f210,f211
PLACE A rot(axis=(-0.68,0.52,-0.52),111.8deg) t=(-97.55,12.51,42.25)mm
PLACE B t=(-104.21,-8.17,14.35)mm fixed
MATE revolute A.f17 <-> B.f128  axis (0,0,-1) through (-87.41,-2.17,44.25)mm
